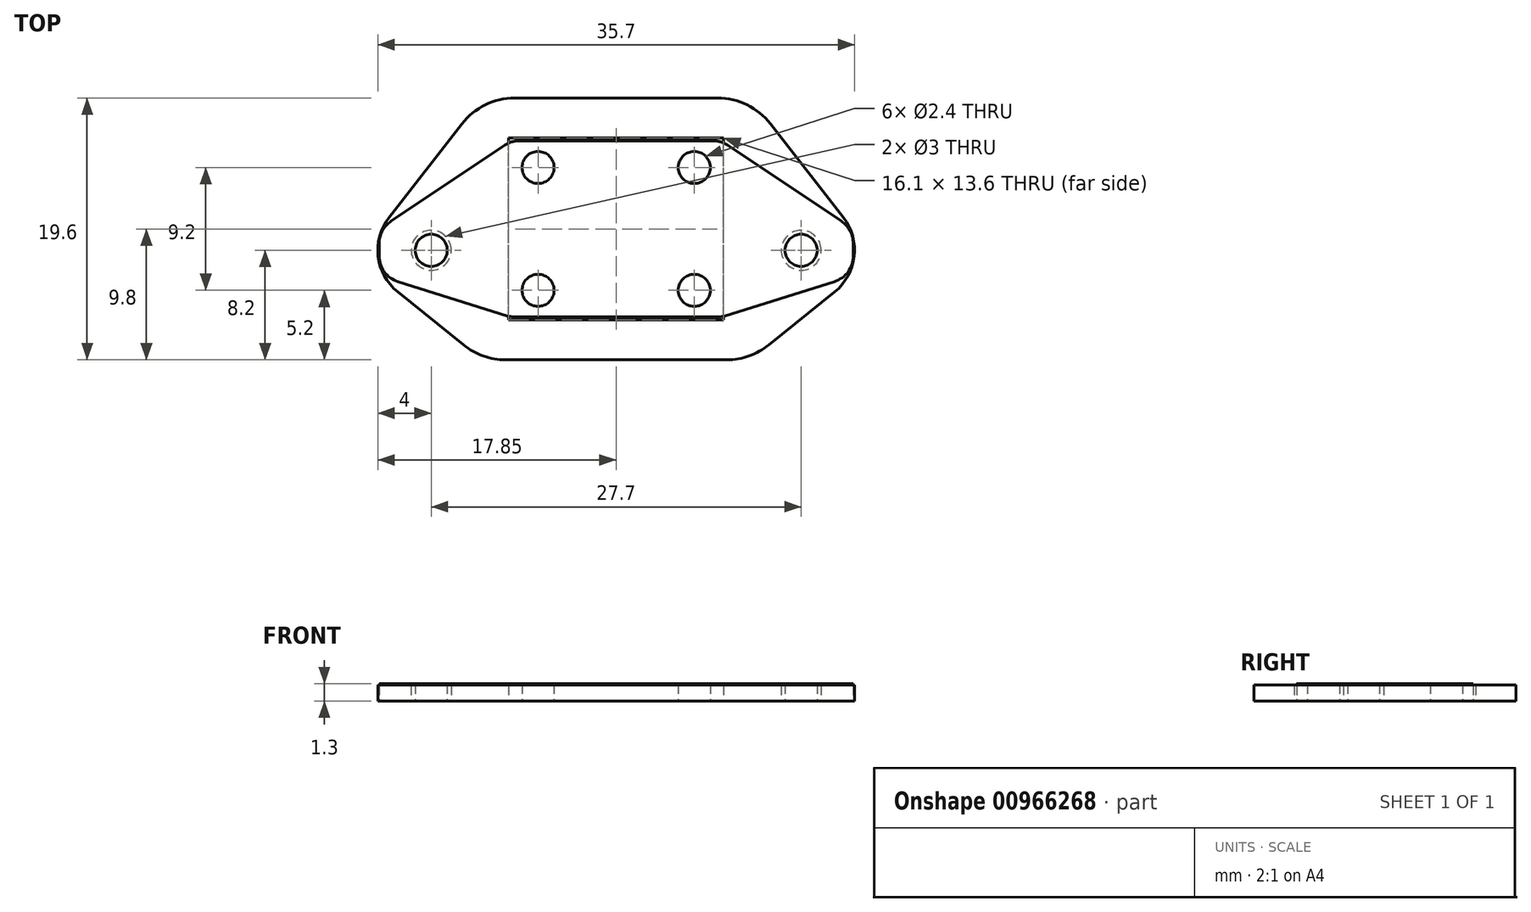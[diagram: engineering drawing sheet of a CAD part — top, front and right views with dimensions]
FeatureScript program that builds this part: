
annotation { "Feature Type Name" : "Feature", "Feature Type Description" : "" }
export const myFeature = defineFeature(function(context is Context, id is Id, definition is map)
    precondition{}
    {
        {
            var Q0;
            Q0=qCreatedBy(makeId("Top.planeOp"),FACE);
            var sketch = newSketch(context, id + "F0", { "sketchPlane" : qUnion([Q0])});
            skLineSegment(sketch, "E0.bottom", {"start": v(0, 0) * mm, "end": v(15.7, 0) * mm, "construction": true});
            skLineSegment(sketch, "E0.top", {"start": v(0, 13.2) * mm, "end": v(15.7, 13.2) * mm, "construction": true});
            skLineSegment(sketch, "E0.left", {"start": v(0, 0) * mm, "end": v(0, 13.2) * mm, "construction": true});
            skLineSegment(sketch, "E0.right", {"start": v(15.7, 0) * mm, "end": v(15.7, 13.2) * mm, "construction": true});
            skCircle(sketch, "E1", {"center": v(2, 11.2) * mm, "radius": 2 * mm});
            skLineSegment(sketch, "E2", {"start": v(7.85, 13.2) * mm, "end": v(7.85, 0) * mm, "construction": true});
            skLineSegment(sketch, "E3", {"start": v(0, 6.6) * mm, "end": v(15.7, 6.6) * mm, "construction": true});
            skCircle(sketch, "E4.MirrorC", {"center": v(2, 2) * mm, "radius": 2 * mm});
            skCircle(sketch, "E5.MirrorC", {"center": v(13.7, 11.2) * mm, "radius": 2 * mm});
            skCircle(sketch, "E6.MirrorC", {"center": v(13.7, 2) * mm, "radius": 2 * mm});
            skCircle(sketch, "E7", {"center": v(2, 11.2) * mm, "radius": 1 * mm});
            skCircle(sketch, "E8.MirrorC", {"center": v(2, 2) * mm, "radius": 1 * mm});
            skCircle(sketch, "E9.MirrorC", {"center": v(13.7, 11.2) * mm, "radius": 1 * mm});
            skCircle(sketch, "E10.MirrorC", {"center": v(13.7, 2) * mm, "radius": 1 * mm});
            skLineSegment(sketch, "E11", {"start": v(21.7, 0) * mm, "end": v(21.7, 13.2) * mm, "construction": true});
            skPoint(sketch, "E12", {"position": v(21.7, 5) * mm});
            skPoint(sketch, "E13.MirrorP", {"position": v(-6, 5) * mm});
            skSolve(sketch);
        }
        {
            var Q0;
            Q0=qCreatedBy(makeId("Top.planeOp"),FACE);
            var sketch = newSketch(context, id + "F1", { "sketchPlane" : qUnion([Q0])});
            skPoint(sketch, "E14.0", {"position": v(-6, 5) * mm});
            skPoint(sketch, "E15.0", {"position": v(2, 11.2) * mm});
            skPoint(sketch, "E16.0", {"position": v(13.7, 11.2) * mm});
            skPoint(sketch, "E17.0", {"position": v(13.7, 2) * mm});
            skPoint(sketch, "E18.0", {"position": v(2, 2) * mm});
            skPoint(sketch, "E19.0", {"position": v(21.7, 5) * mm});
            skLineSegment(sketch, "E20.0", {"start": v(0, 13.2) * mm, "end": v(15.7, 13.2) * mm});
            skLineSegment(sketch, "E21.0", {"start": v(0, 0) * mm, "end": v(15.7, 0) * mm});
            skLineSegment(sketch, "E22", {"start": v(25.6, 6.58) * mm, "end": v(25.6, 3.1) * mm});
            skLineSegment(sketch, "E23", {"start": v(25.6, 3.1) * mm, "end": v(15.7, 0) * mm});
            skLineSegment(sketch, "E24", {"start": v(25.6, 6.58) * mm, "end": v(15.7, 13.2) * mm});
            skLineSegment(sketch, "E25.MirrorCS", {"start": v(-9.9, 6.58) * mm, "end": v(0, 13.2) * mm});
            skLineSegment(sketch, "E26.MirrorCS", {"start": v(-9.9, 6.58) * mm, "end": v(-9.9, 3.1) * mm});
            skLineSegment(sketch, "E27.MirrorCS", {"start": v(-9.9, 3.1) * mm, "end": v(0, 0) * mm});
            skSolve(sketch);
        }
        {
            var Q0;
            Q0=makeQuery(id+"F1.imprint","IMPRINT",FACE,{"disambiguationData":[TD([[makeQuery(id+"F1.imprint","IMPRINT",EDGE,{"derivedFrom":sQuery(id+"F1.wireOp",EDGE,"E20.0")}),-1.0]])]});
            extrude(context, id + "F2", {"entities" : qUnion([Q0]), "depth" : 1.3 * mm, "offsetDistance" : 25 * mm});
        }
        {
            var Q0;
            Q0=sQuery(id+"F0.wireOp",VERTEX,"E5.MirrorC.center");
            var Q1;
            Q1=sQuery(id+"F0.wireOp",VERTEX,"E1.center");
            var Q2;
            Q2=sQuery(id+"F0.wireOp",VERTEX,"E13.MirrorP");
            var Q3;
            Q3=sQuery(id+"F0.wireOp",VERTEX,"E4.MirrorC.center");
            var Q4;
            Q4=sQuery(id+"F0.wireOp",VERTEX,"E6.MirrorC.center");
            var Q5;
            Q5=sQuery(id+"F0.wireOp",VERTEX,"E12");
            var Q6;
            Q6=makeQuery(id+"F2.opExtrude","SWEPT_BODY",BODY,{"disambiguationData":[OSD([sQuery(id+"F1.wireOp",EDGE,"E20.0"),sQuery(id+"F1.wireOp",EDGE,"E21.0"),sQuery(id+"F1.wireOp",EDGE,"E22"),sQuery(id+"F1.wireOp",EDGE,"E23"),sQuery(id+"F1.wireOp",EDGE,"E24"),sQuery(id+"F1.wireOp",EDGE,"E25.MirrorCS"),sQuery(id+"F1.wireOp",EDGE,"E26.MirrorCS"),sQuery(id+"F1.wireOp",EDGE,"E27.MirrorCS")])]});
            hole(context, id + "F3", {"style" : HoleStyle.SIMPLE, "endStyle" : HoleEndStyle.THROUGH, "oppositeDirection" : true, "standardTappedOrClearance" : lookupTablePath({ "fit" : "Normal", "standard" : "ISO", "size" : "M2", "type" : "Clearance" }), "standardBlindInLast" : lookupTablePath({ "fit" : "Normal", "standard" : "ISO", "engagement" : "75%", "pitch" : "0.25 mm", "size" : "M2", "type" : "Clearance & tapped" }), "holeDiameter" : 2.4 * mm, "majorDiameter" : 5 * mm, "isTappedThrough" : true, "tappedDepth" : 12 * mm, "tapClearance" : 3, "locations" : qUnion([Q0, Q1, Q2, Q3, Q4, Q5]), "scope" : qUnion([Q6])});
        }
        {
            var Q0;
            Q0=makeQuery(id+"F2.opExtrude","SWEPT_EDGE",EDGE,{"disambiguationData":[OSD([sQuery(id+"F1.wireOp",EDGE,"E26.MirrorCS"),sQuery(id+"F1.wireOp",EDGE,"E27.MirrorCS")])]});
            var Q1;
            Q1=makeQuery(id+"F2.opExtrude","SWEPT_EDGE",EDGE,{"disambiguationData":[OSD([sQuery(id+"F1.wireOp",EDGE,"E25.MirrorCS"),sQuery(id+"F1.wireOp",EDGE,"E26.MirrorCS")])]});
            var Q2;
            Q2=makeQuery(id+"F2.opExtrude","SWEPT_EDGE",EDGE,{"disambiguationData":[OSD([sQuery(id+"F1.wireOp",EDGE,"E20.0"),sQuery(id+"F1.wireOp",EDGE,"E25.MirrorCS")])]});
            var Q3;
            Q3=makeQuery(id+"F2.opExtrude","SWEPT_EDGE",EDGE,{"disambiguationData":[OSD([sQuery(id+"F1.wireOp",EDGE,"E21.0"),sQuery(id+"F1.wireOp",EDGE,"E27.MirrorCS")])]});
            var Q4;
            Q4=makeQuery(id+"F2.opExtrude","SWEPT_EDGE",EDGE,{"disambiguationData":[OSD([sQuery(id+"F1.wireOp",EDGE,"E21.0"),sQuery(id+"F1.wireOp",EDGE,"E23")])]});
            var Q5;
            Q5=makeQuery(id+"F2.opExtrude","SWEPT_EDGE",EDGE,{"disambiguationData":[OSD([sQuery(id+"F1.wireOp",EDGE,"E22"),sQuery(id+"F1.wireOp",EDGE,"E23")])]});
            var Q6;
            Q6=makeQuery(id+"F2.opExtrude","SWEPT_EDGE",EDGE,{"disambiguationData":[OSD([sQuery(id+"F1.wireOp",EDGE,"E22"),sQuery(id+"F1.wireOp",EDGE,"E24")])]});
            var Q7;
            Q7=makeQuery(id+"F2.opExtrude","SWEPT_EDGE",EDGE,{"disambiguationData":[OSD([sQuery(id+"F1.wireOp",EDGE,"E20.0"),sQuery(id+"F1.wireOp",EDGE,"E24")])]});
            fillet(context, id + "F4", {"entities" : qUnion([Q0, Q1, Q2, Q3, Q4, Q5, Q6, Q7]), "radius" : 2 * mm, "tangentPropagation" : true, "allowEdgeOverflow" : false});
        }
        {
            var Q0;
            Q0=qCreatedBy(makeId("Top.planeOp"),FACE);
            var sketch = newSketch(context, id + "F5", { "sketchPlane" : qUnion([Q0])});
            skPoint(sketch, "E28.0", {"position": v(-6, 5) * mm});
            skPoint(sketch, "E29.0", {"position": v(21.7, 5) * mm});
            skLineSegment(sketch, "E30.0", {"start": v(0, 13.2) * mm, "end": v(15.7, 13.2) * mm, "construction": true});
            skLineSegment(sketch, "E31.0", {"start": v(0, 0) * mm, "end": v(0, 13.2) * mm, "construction": true});
            skLineSegment(sketch, "E32.0", {"start": v(0, 0) * mm, "end": v(15.7, 0) * mm, "construction": true});
            skLineSegment(sketch, "E33.0", {"start": v(15.7, 0) * mm, "end": v(15.7, 13.2) * mm, "construction": true});
            skLineSegment(sketch, "E34.0", {"start": v(-0.2, 13.4) * mm, "end": v(15.9, 13.4) * mm});
            skLineSegment(sketch, "E34.1", {"start": v(-0.2, -0.2) * mm, "end": v(-0.2, 13.4) * mm});
            skLineSegment(sketch, "E34.2", {"start": v(-0.2, -0.2) * mm, "end": v(15.9, -0.2) * mm});
            skLineSegment(sketch, "E34.3", {"start": v(15.9, -0.2) * mm, "end": v(15.9, 13.4) * mm});
            skCircle(sketch, "E35", {"center": v(-6, 5) * mm, "radius": 4 * mm});
            skCircle(sketch, "E36", {"center": v(21.7, 5) * mm, "radius": 4 * mm});
            skLineSegment(sketch, "E37.0", {"start": v(-2.2, 16.4) * mm, "end": v(17.9, 16.4) * mm});
            skLineSegment(sketch, "E38.0", {"start": v(-2.2, -3.2) * mm, "end": v(17.9, -3.2) * mm});
            skCircle(sketch, "E39", {"center": v(-6, 5) * mm, "radius": 1.5 * mm});
            skCircle(sketch, "E40", {"center": v(21.7, 5) * mm, "radius": 1.5 * mm});
            skPoint(sketch, "E41.0", {"position": v(7.85, 6.6) * mm});
            skLineSegment(sketch, "E42", {"start": v(-2.2, 16.4) * mm, "end": v(-9.16, 7.46) * mm});
            skLineSegment(sketch, "E43", {"start": v(-2.2, -3.2) * mm, "end": v(-8.51, 1.89) * mm});
            skLineSegment(sketch, "E44", {"start": v(17.9, -3.2) * mm, "end": v(24.21, 1.89) * mm});
            skLineSegment(sketch, "E45", {"start": v(17.9, 16.4) * mm, "end": v(24.86, 7.46) * mm});
            skSolve(sketch);
        }
        {
            var Q0;
            Q0=makeQuery(id+"F5.imprint","IMPRINT",FACE,{"disambiguationData":[TD([[makeQuery(id+"F5.imprint","IMPRINT",EDGE,{"derivedFrom":sQuery(id+"F5.wireOp",EDGE,"E39")}),-1.0]])]});
            var Q1;
            Q1=makeQuery(id+"F5.imprint","IMPRINT",FACE,{"disambiguationData":[TD([[makeQuery(id+"F5.imprint","IMPRINT",EDGE,{"derivedFrom":sQuery(id+"F5.wireOp",EDGE,"E34.0")}),1.0]])]});
            var Q2;
            Q2=makeQuery(id+"F5.imprint","IMPRINT",FACE,{"disambiguationData":[TD([[makeQuery(id+"F5.imprint","IMPRINT",EDGE,{"derivedFrom":sQuery(id+"F5.wireOp",EDGE,"E40")}),-1.0]])]});
            extrude(context, id + "F6", {"entities" : qUnion([Q0, Q1, Q2]), "depth" : 1.2 * mm, "offsetDistance" : 25 * mm});
        }
        {
            var Q0;
            Q0=makeQuery(id+"F6.opExtrude","SWEPT_EDGE",EDGE,{"disambiguationData":[OSD([sQuery(id+"F5.wireOp",EDGE,"E38.0"),sQuery(id+"F5.wireOp",EDGE,"E43")])]});
            var Q1;
            Q1=makeQuery(id+"F6.opExtrude","SWEPT_EDGE",EDGE,{"disambiguationData":[OSD([sQuery(id+"F5.wireOp",EDGE,"E38.0"),sQuery(id+"F5.wireOp",EDGE,"E44")])]});
            var Q2;
            Q2=makeQuery(id+"F6.opExtrude","SWEPT_EDGE",EDGE,{"disambiguationData":[OSD([sQuery(id+"F5.wireOp",EDGE,"E37.0"),sQuery(id+"F5.wireOp",EDGE,"E45")])]});
            var Q3;
            Q3=makeQuery(id+"F6.opExtrude","SWEPT_EDGE",EDGE,{"disambiguationData":[OSD([sQuery(id+"F5.wireOp",EDGE,"E37.0"),sQuery(id+"F5.wireOp",EDGE,"E42")])]});
            fillet(context, id + "F7", {"entities" : qUnion([Q0, Q1, Q2, Q3]), "radius" : 5 * mm, "tangentPropagation" : true, "allowEdgeOverflow" : false});
        }
    });
